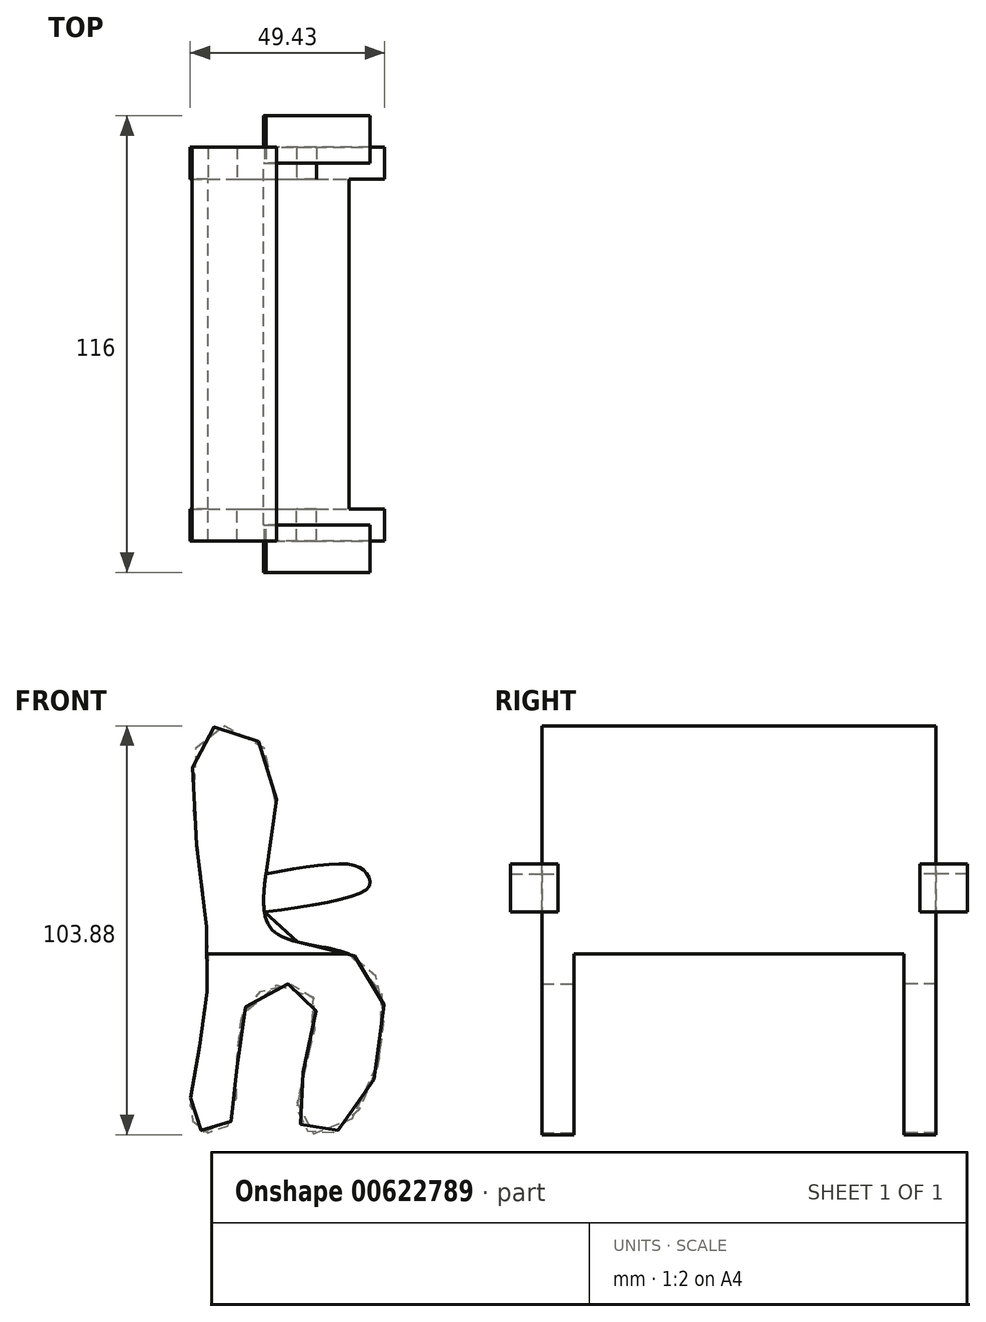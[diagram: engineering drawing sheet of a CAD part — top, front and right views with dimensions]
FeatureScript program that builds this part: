
annotation { "Feature Type Name" : "Feature", "Feature Type Description" : "" }
export const myFeature = defineFeature(function(context is Context, id is Id, definition is map)
    precondition{}
    {
        {
            var Q0;
            Q0=qCreatedBy(makeId("Front.planeOp"),FACE);
            var sketch = newSketch(context, id + "F0", { "sketchPlane" : qUnion([Q0])});
            skFitSpline(sketch, "E0", {"points": [v(-61.08, 33.87) * mm, v(-61.08, -13.75) * mm, v(-63.15, -48.36) * mm, v(-63.45, -66.7) * mm, v(-54.87, -65.52) * mm, v(-50.14, -34.76) * mm, v(-33.87, -33.57) * mm, v(-37.71, -64.34) * mm, v(-25.59, -66.11) * mm, v(-19.37, -26.18) * mm, v(-44.81, -15.83) * mm, v(-44.22, 25.88) * mm, v(-61.08, 33.87) * mm]});
            skSolve(sketch);
        }
        {
            var Q0;
            Q0=makeQuery(id+"F0.imprint","IMPRINT",FACE,{"disambiguationData":[TD([[makeQuery(id+"F0.imprint","IMPRINT",EDGE,{"derivedFrom":sQuery(id+"F0.wireOp",EDGE,"E0")}),1.0]])]});
            extrude(context, id + "F1", {"entities" : qUnion([Q0]), "depth" : 100 * mm, "offsetDistance" : 25 * mm});
        }
        {
            var Q0;
            Q0=qCreatedBy(makeId("Right.planeOp"),FACE);
            var sketch = newSketch(context, id + "F2", { "sketchPlane" : qUnion([Q0])});
            skLineSegment(sketch, "E1.bottom", {"start": v(-92.47, -22.65) * mm, "end": v(-8.08, -22.65) * mm});
            skLineSegment(sketch, "E1.top", {"start": v(-92.47, -75.27) * mm, "end": v(-8.08, -75.27) * mm});
            skLineSegment(sketch, "E1.left", {"start": v(-92.47, -22.65) * mm, "end": v(-92.47, -75.27) * mm});
            skLineSegment(sketch, "E1.right", {"start": v(-8.08, -22.65) * mm, "end": v(-8.08, -75.27) * mm});
            skSolve(sketch);
        }
        {
            var Q0;
            Q0=makeQuery(id+"F2.imprint","IMPRINT",FACE,{"disambiguationData":[TD([[makeQuery(id+"F2.imprint","IMPRINT",EDGE,{"derivedFrom":sQuery(id+"F2.wireOp",EDGE,"E1.bottom")}),-1.0]])]});
            extrude(context, id + "F3", {"entities" : qUnion([Q0]), "operationType" : NewBodyOperationType.REMOVE, "oppositeDirection" : true, "depth" : 89.9 * mm, "offsetDistance" : 25 * mm});
        }
        {
            var Q0;
            Q0=makeQuery(id+"F1.opExtrude","CAP_FACE",FACE,{"disambiguationData":[OSD([sQuery(id+"F0.wireOp",EDGE,"E0")])],"isStart":true});
            var sketch = newSketch(context, id + "F4", { "sketchPlane" : qUnion([Q0])});
            skFitSpline(sketch, "E2", {"points": [v(48.96, -2.91) * mm, v(23.96, 0) * mm, v(20.02, -2.54) * mm, v(19.83, -5.73) * mm, v(49.9, -12.5) * mm], "startDerivative": vector(-87.55, 16.7) * mm, "endDerivative": vector(108.23, -14.03) * mm});
            skSolve(sketch);
        }
        {
            var Q0;
            {var subQ0=sQuery(id+"F4.wireOp",EDGE,"E2");var subQ1=makeQuery(id+"F1.opExtrude","CAP_EDGE",EDGE,{"disambiguationData":[OSD([sQuery(id+"F0.wireOp",EDGE,"E0")])],"isStart":true});var subQ2=makeQuery(id+"F4.imprint","INTERSECT",VERTEX,{"disambiguationData":[OD(0.0)],"derivedFrom":[subQ1,subQ0]});Q0=makeQuery(id+"F4.imprint","IMPRINT",FACE,{"disambiguationData":[TD([[makeQuery(id+"F4.imprint","IMPRINT",EDGE,{"disambiguationData":[TD([[subQ2,1.0]])],"derivedFrom":subQ0}),1.0]])]});}
            extrude(context, id + "F5", {"entities" : qUnion([Q0]), "operationType" : NewBodyOperationType.ADD, "depth" : 8 * mm, "offsetDistance" : 25 * mm, "hasSecondDirection" : true, "secondDirectionOppositeDirection" : true, "secondDirectionDepth" : 4 * mm});
        }
        {
            var Q0;
            Q0=qCreatedBy(makeId("Front.planeOp"),FACE);
            cPlane(context, id + "F6", {"entities" : qUnion([Q0]), "cplaneType" : CPlaneType.OFFSET, "offset" : 50 * mm, "width" : 150 * mm, "height" : 150 * mm});
        }
        {
            var Q0;
            Q0=makeQuery(id+"F1.opExtrude","SWEPT_BODY",BODY,{"disambiguationData":[OSD([sQuery(id+"F0.wireOp",EDGE,"E0")])]});
            var Q1;
            Q1=qCreatedBy(id+"F6.planeOp",FACE);
            mirror(context, id + "F7", {"operationType" : NewBodyOperationType.ADD, "entities" : qUnion([Q0]), "mirrorPlane" : qUnion([Q1])});
        }
    });
